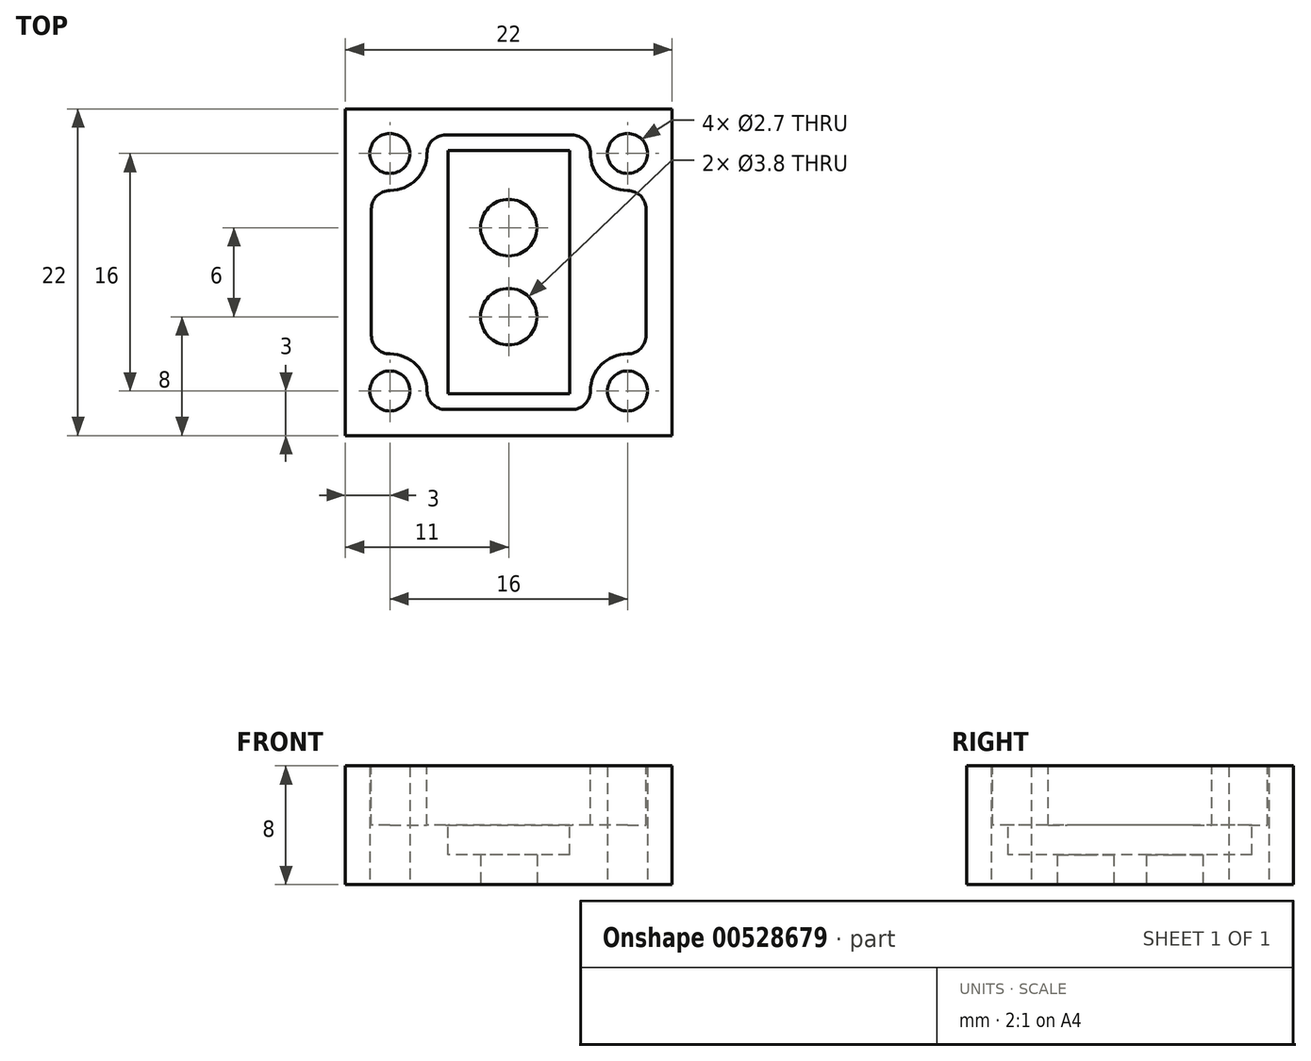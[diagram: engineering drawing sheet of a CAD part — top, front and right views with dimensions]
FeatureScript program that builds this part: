
annotation { "Feature Type Name" : "Feature", "Feature Type Description" : "" }
export const myFeature = defineFeature(function(context is Context, id is Id, definition is map)
    precondition{}
    {
        {
            var Q0;
            Q0=qCreatedBy(makeId("Top.planeOp"),FACE);
            var sketch = newSketch(context, id + "F0", { "sketchPlane" : qUnion([Q0])});
            skLineSegment(sketch, "E0.bottom", {"start": v(11, 11) * mm, "end": v(-11, 11) * mm});
            skLineSegment(sketch, "E0.top", {"start": v(11, -11) * mm, "end": v(-11, -11) * mm});
            skLineSegment(sketch, "E0.left", {"start": v(11, 11) * mm, "end": v(11, -11) * mm});
            skLineSegment(sketch, "E0.right", {"start": v(-11, 11) * mm, "end": v(-11, -11) * mm});
            skPoint(sketch, "E0.middle", {"position": v(0, 0) * mm});
            skLineSegment(sketch, "E1", {"start": v(0, 0) * mm, "end": v(-8, 0) * mm, "construction": true});
            skLineSegment(sketch, "E2", {"start": v(-8, 0) * mm, "end": v(-8, 8) * mm, "construction": true});
            skLineSegment(sketch, "E3", {"start": v(0, 0) * mm, "end": v(0, 3) * mm, "construction": true});
            skCircle(sketch, "E4", {"center": v(-8, 8) * mm, "radius": 1.35 * mm});
            skCircle(sketch, "E5", {"center": v(0, 3) * mm, "radius": 1.9 * mm});
            skCircle(sketch, "E6.0.1.0", {"center": v(-8, -8) * mm, "radius": 1.35 * mm});
            skCircle(sketch, "E6.1.0.0", {"center": v(8, 8) * mm, "radius": 1.35 * mm});
            skCircle(sketch, "E6.1.1.0", {"center": v(8, -8) * mm, "radius": 1.35 * mm});
            skLineSegment(sketch, "E6.direction1", {"start": v(-8, 8) * mm, "end": v(8, 8) * mm, "construction": true});
            skLineSegment(sketch, "E6.direction2", {"start": v(-8, 8) * mm, "end": v(-8, -8) * mm, "construction": true});
            skCircle(sketch, "E7.MirrorC", {"center": v(0, -3) * mm, "radius": 1.9 * mm});
            skSolve(sketch);
        }
        {
            var Q0;
            Q0=makeQuery(id+"F0.imprint","IMPRINT",FACE,{"disambiguationData":[TD([[makeQuery(id+"F0.imprint","IMPRINT",EDGE,{"derivedFrom":sQuery(id+"F0.wireOp",EDGE,"E0.bottom")}),1.0]])]});
            extrude(context, id + "F1", {"entities" : qUnion([Q0]), "depth" : 8 * mm, "offsetDistance" : 25 * mm});
        }
        {
            var Q0;
            Q0=makeQuery(id+"F1.opExtrude","CAP_FACE",FACE,{"disambiguationData":[OSD([sQuery(id+"F0.wireOp",EDGE,"E0.bottom"),sQuery(id+"F0.wireOp",EDGE,"E0.top"),sQuery(id+"F0.wireOp",EDGE,"E0.left"),sQuery(id+"F0.wireOp",EDGE,"E0.right"),sQuery(id+"F0.wireOp",EDGE,"E4"),sQuery(id+"F0.wireOp",EDGE,"E5"),sQuery(id+"F0.wireOp",EDGE,"E6.0.1.0"),sQuery(id+"F0.wireOp",EDGE,"E6.1.0.0"),sQuery(id+"F0.wireOp",EDGE,"E6.1.1.0"),sQuery(id+"F0.wireOp",EDGE,"E7.MirrorC")])],"isStart":false});
            var sketch = newSketch(context, id + "F2", { "sketchPlane" : qUnion([Q0])});
            skLineSegment(sketch, "E8.bottom", {"start": v(4.1, 8.2) * mm, "end": v(-4.1, 8.2) * mm});
            skLineSegment(sketch, "E8.top", {"start": v(4.1, -8.2) * mm, "end": v(-4.1, -8.2) * mm});
            skLineSegment(sketch, "E8.left", {"start": v(4.1, 8.2) * mm, "end": v(4.1, -8.2) * mm});
            skLineSegment(sketch, "E8.right", {"start": v(-4.1, 8.2) * mm, "end": v(-4.1, -8.2) * mm});
            skPoint(sketch, "E8.middle", {"position": v(0, 0) * mm});
            skCircle(sketch, "E9", {"center": v(-8, 8) * mm, "radius": 2.5 * mm, "construction": true});
            skLineSegment(sketch, "E10", {"start": v(-8, 8) * mm, "end": v(-8, 0) * mm, "construction": true});
            skCircle(sketch, "E11", {"center": v(0, 0) * mm, "radius": 8 * mm, "construction": true});
            skLineSegment(sketch, "E12.bottom", {"start": v(-9.25, 9.25) * mm, "end": v(9.25, 9.25) * mm, "construction": true});
            skLineSegment(sketch, "E12.top", {"start": v(-9.25, -9.25) * mm, "end": v(9.25, -9.25) * mm, "construction": true});
            skLineSegment(sketch, "E12.left", {"start": v(-9.25, 9.25) * mm, "end": v(-9.25, -9.25) * mm, "construction": true});
            skLineSegment(sketch, "E12.right", {"start": v(9.25, 9.25) * mm, "end": v(9.25, -9.25) * mm, "construction": true});
            skArc(sketch, "E13", {"start": v(-8, 5.5) * mm, "mid": v(-6.23, 6.23) * mm, "end": v(-5.5, 8) * mm});
            skLineSegment(sketch, "E14", {"start": v(-5.5, 8) * mm, "end": v(-5.5, 9.25) * mm});
            skLineSegment(sketch, "E15", {"start": v(-8, 5.5) * mm, "end": v(-9.25, 5.5) * mm});
            skLineSegment(sketch, "E16.MirrorCS", {"start": v(5.5, 8) * mm, "end": v(5.5, 9.25) * mm});
            skLineSegment(sketch, "E17.MirrorCS", {"start": v(8, 5.5) * mm, "end": v(9.25, 5.5) * mm});
            skArc(sketch, "E18.MirrorCS", {"start": v(8, 5.5) * mm, "mid": v(6.23, 6.23) * mm, "end": v(5.5, 8) * mm});
            skLineSegment(sketch, "E19.MirrorCS", {"start": v(-8, -5.5) * mm, "end": v(-9.25, -5.5) * mm});
            skArc(sketch, "E20.MirrorCS", {"start": v(-8, -5.5) * mm, "mid": v(-6.23, -6.23) * mm, "end": v(-5.5, -8) * mm});
            skLineSegment(sketch, "E21.MirrorCS", {"start": v(-5.5, -8) * mm, "end": v(-5.5, -9.25) * mm});
            skLineSegment(sketch, "E22.MirrorCS", {"start": v(5.5, -8) * mm, "end": v(5.5, -9.25) * mm});
            skLineSegment(sketch, "E23.MirrorCS", {"start": v(8, -5.5) * mm, "end": v(9.25, -5.5) * mm});
            skArc(sketch, "E24.MirrorCS", {"start": v(8, -5.5) * mm, "mid": v(6.23, -6.23) * mm, "end": v(5.5, -8) * mm});
            skLineSegment(sketch, "E25", {"start": v(-5.5, 9.25) * mm, "end": v(5.5, 9.25) * mm});
            skLineSegment(sketch, "E26", {"start": v(9.25, 5.5) * mm, "end": v(9.25, -5.5) * mm});
            skLineSegment(sketch, "E27", {"start": v(5.5, -9.25) * mm, "end": v(-5.5, -9.25) * mm});
            skLineSegment(sketch, "E28", {"start": v(-9.25, -5.5) * mm, "end": v(-9.25, 5.5) * mm});
            skSolve(sketch);
        }
        {
            var Q0;
            Q0=makeQuery(id+"F2.imprint","IMPRINT",FACE,{"disambiguationData":[TD([[makeQuery(id+"F2.imprint","IMPRINT",EDGE,{"derivedFrom":sQuery(id+"F2.wireOp",EDGE,"E8.bottom")}),1.0]])]});
            extrude(context, id + "F3", {"entities" : qUnion([Q0]), "operationType" : NewBodyOperationType.REMOVE, "oppositeDirection" : true, "depth" : 6 * mm, "offsetDistance" : 25 * mm});
        }
        {
            var Q0;
            Q0 = qSketchRegion(id + "F2", true);
            extrude(context, id + "F4", {"entities" : qUnion([Q0]), "operationType" : NewBodyOperationType.REMOVE, "oppositeDirection" : true, "depth" : 4 * mm, "offsetDistance" : 25 * mm});
        }
        {
            var Q0;
            Q0=makeQuery(id+"F4.boolean.opBoolean","COPY",EDGE,{"derivedFrom":makeQuery(id+"F4.opExtrude","SWEPT_EDGE",EDGE,{"disambiguationData":[OSD([sQuery(id+"F2.wireOp",EDGE,"E15"),sQuery(id+"F2.wireOp",EDGE,"E28")])]})});
            var Q1;
            Q1=makeQuery(id+"F4.boolean.opBoolean","COPY",EDGE,{"derivedFrom":makeQuery(id+"F4.opExtrude","SWEPT_EDGE",EDGE,{"disambiguationData":[OSD([sQuery(id+"F2.wireOp",EDGE,"E14"),sQuery(id+"F2.wireOp",EDGE,"E25")])]})});
            var Q2;
            Q2=makeQuery(id+"F4.boolean.opBoolean","COPY",EDGE,{"derivedFrom":makeQuery(id+"F4.opExtrude","SWEPT_EDGE",EDGE,{"disambiguationData":[OSD([sQuery(id+"F2.wireOp",EDGE,"E16.MirrorCS"),sQuery(id+"F2.wireOp",EDGE,"E25")])]})});
            var Q3;
            Q3=makeQuery(id+"F4.boolean.opBoolean","COPY",EDGE,{"derivedFrom":makeQuery(id+"F4.opExtrude","SWEPT_EDGE",EDGE,{"disambiguationData":[OSD([sQuery(id+"F2.wireOp",EDGE,"E17.MirrorCS"),sQuery(id+"F2.wireOp",EDGE,"E26")])]})});
            var Q4;
            Q4=makeQuery(id+"F4.boolean.opBoolean","COPY",EDGE,{"derivedFrom":makeQuery(id+"F4.opExtrude","SWEPT_EDGE",EDGE,{"disambiguationData":[OSD([sQuery(id+"F2.wireOp",EDGE,"E19.MirrorCS"),sQuery(id+"F2.wireOp",EDGE,"E28")])]})});
            var Q5;
            Q5=makeQuery(id+"F4.boolean.opBoolean","COPY",EDGE,{"derivedFrom":makeQuery(id+"F4.opExtrude","SWEPT_EDGE",EDGE,{"disambiguationData":[OSD([sQuery(id+"F2.wireOp",EDGE,"E21.MirrorCS"),sQuery(id+"F2.wireOp",EDGE,"E27")])]})});
            var Q6;
            Q6=makeQuery(id+"F4.boolean.opBoolean","COPY",EDGE,{"derivedFrom":makeQuery(id+"F4.opExtrude","SWEPT_EDGE",EDGE,{"disambiguationData":[OSD([sQuery(id+"F2.wireOp",EDGE,"E22.MirrorCS"),sQuery(id+"F2.wireOp",EDGE,"E27")])]})});
            var Q7;
            Q7=makeQuery(id+"F4.boolean.opBoolean","COPY",EDGE,{"derivedFrom":makeQuery(id+"F4.opExtrude","SWEPT_EDGE",EDGE,{"disambiguationData":[OSD([sQuery(id+"F2.wireOp",EDGE,"E23.MirrorCS"),sQuery(id+"F2.wireOp",EDGE,"E26")])]})});
            fillet(context, id + "F5", {"entities" : qUnion([Q0, Q1, Q2, Q3, Q4, Q5, Q6, Q7]), "tangentPropagation" : true, "radius" : 1.25 * mm, "defaultsChanged" : true, "vertexSettings" : [], "allowEdgeOverflow" : false});
        }
    });
